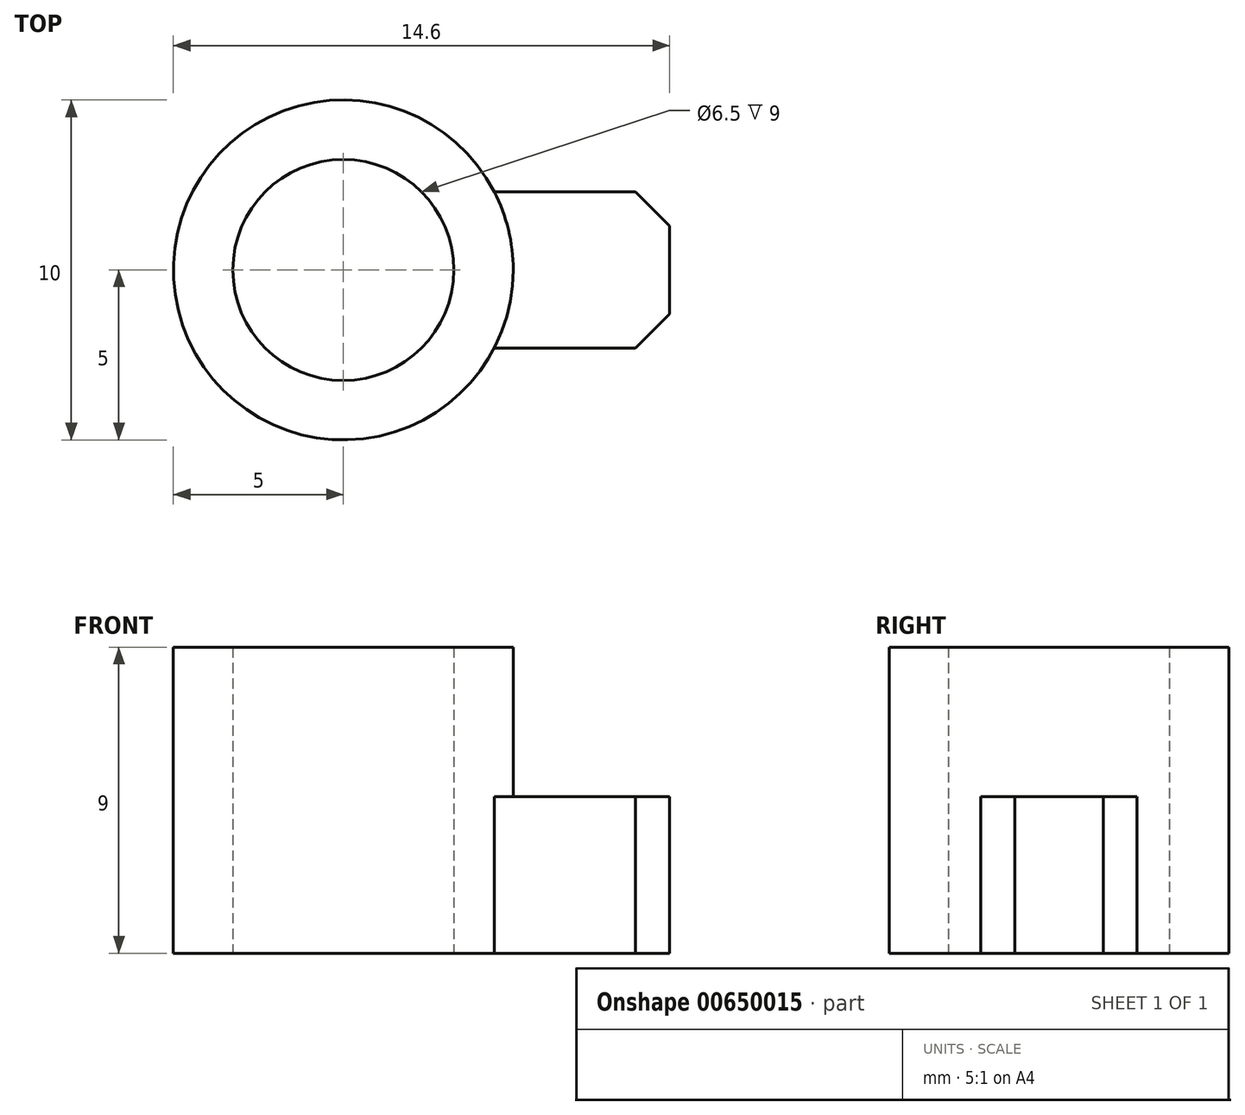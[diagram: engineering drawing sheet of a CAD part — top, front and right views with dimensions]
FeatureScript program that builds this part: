
annotation { "Feature Type Name" : "Feature", "Feature Type Description" : "" }
export const myFeature = defineFeature(function(context is Context, id is Id, definition is map)
    precondition{}
    {
        {
            var Q0;
            Q0=qCreatedBy(makeId("Top.planeOp"),FACE);
            var sketch = newSketch(context, id + "F0", { "sketchPlane" : qUnion([Q0])});
            skPoint(sketch, "E0.middle", {"position": v(0, 0) * mm});
            skLineSegment(sketch, "E1.bottom", {"start": v(9.6, -2.3) * mm, "end": v(0.4, -2.3) * mm});
            skLineSegment(sketch, "E1.top", {"start": v(9.6, 2.3) * mm, "end": v(0.4, 2.3) * mm});
            skLineSegment(sketch, "E1.left", {"start": v(9.6, -2.3) * mm, "end": v(9.6, 2.3) * mm});
            skLineSegment(sketch, "E1.right", {"start": v(0.4, -2.3) * mm, "end": v(0.4, 2.3) * mm});
            skPoint(sketch, "E1.middle", {"position": v(5, 0) * mm});
            skCircle(sketch, "E2", {"center": v(0, 0) * mm, "radius": 3.25 * mm});
            skCircle(sketch, "E3", {"center": v(0, 0) * mm, "radius": 5 * mm});
            skSolve(sketch);
        }
        {
            var Q0;
            {var subQ0=sQuery(id+"F0.wireOp",EDGE,"E3");var subQ1=sQuery(id+"F0.wireOp",EDGE,"E1.bottom");var subQ2=makeQuery(id+"F0.imprint","INTERSECT",VERTEX,{"derivedFrom":[subQ1,subQ0]});Q0=makeQuery(id+"F0.imprint","IMPRINT",FACE,{"disambiguationData":[TD([[makeQuery(id+"F0.imprint","IMPRINT",EDGE,{"disambiguationData":[TD([[subQ2,-1.0]])],"derivedFrom":subQ1}),1.0]])]});}
            var Q1;
            {var subQ0=sQuery(id+"F0.wireOp",EDGE,"E3");var subQ1=sQuery(id+"F0.wireOp",EDGE,"E1.bottom");var subQ2=makeQuery(id+"F0.imprint","INTERSECT",VERTEX,{"derivedFrom":[subQ1,subQ0]});Q1=makeQuery(id+"F0.imprint","IMPRINT",FACE,{"disambiguationData":[TD([[makeQuery(id+"F0.imprint","IMPRINT",EDGE,{"disambiguationData":[TD([[subQ2,-1.0]])],"derivedFrom":subQ1}),-1.0]])]});}
            extrude(context, id + "F1", {"entities" : qUnion([Q0, Q1]), "depth" : 9 * mm, "offsetDistance" : 25 * mm});
        }
        {
            var Q0;
            {var subQ0=sQuery(id+"F0.wireOp",EDGE,"E1.left");Q0=makeQuery(id+"F0.imprint","IMPRINT",FACE,{"disambiguationData":[TD([[makeQuery(id+"F0.imprint","IMPRINT",EDGE,{"derivedFrom":subQ0}),1.0]])]});}
            extrude(context, id + "F2", {"entities" : qUnion([Q0]), "operationType" : NewBodyOperationType.ADD, "depth" : 4.6 * mm, "offsetDistance" : 25 * mm});
        }
        {
            var Q0;
            Q0=makeQuery(id+"F2.opExtrude","SWEPT_EDGE",EDGE,{"disambiguationData":[OSD([sQuery(id+"F0.wireOp",EDGE,"E1.bottom"),sQuery(id+"F0.wireOp",EDGE,"E1.left")])]});
            var Q1;
            Q1=makeQuery(id+"F2.opExtrude","SWEPT_EDGE",EDGE,{"disambiguationData":[OSD([sQuery(id+"F0.wireOp",EDGE,"E1.top"),sQuery(id+"F0.wireOp",EDGE,"E1.left")])]});
            chamfer(context, id + "F3", {"entities" : qUnion([Q0, Q1]), "width" : 1 * mm, "tangentPropagation" : true});
        }
    });
